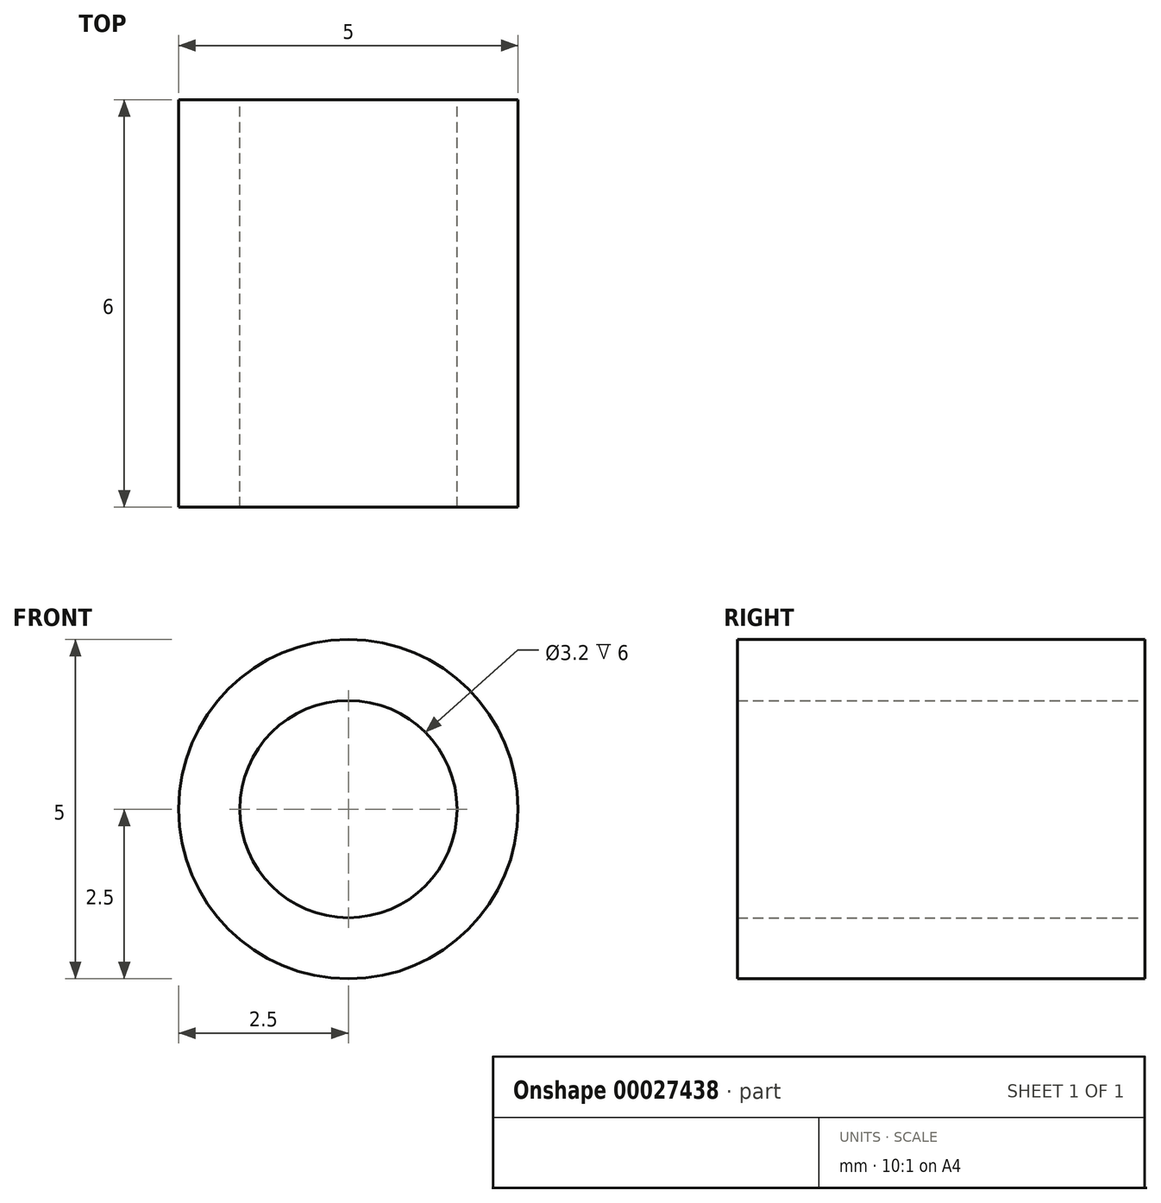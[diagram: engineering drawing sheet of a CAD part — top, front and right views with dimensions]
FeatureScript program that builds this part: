
annotation { "Feature Type Name" : "Feature", "Feature Type Description" : "" }
export const myFeature = defineFeature(function(context is Context, id is Id, definition is map)
    precondition{}
    {
        {
            var Q0;
            Q0=qCreatedBy(makeId("Front.planeOp"),FACE);
            var sketch = newSketch(context, id + "F0", { "sketchPlane" : qUnion([Q0])});
            skCircle(sketch, "E0", {"center": v(0, 0) * mm, "radius": 2.5 * mm});
            skCircle(sketch, "E1", {"center": v(0, 0) * mm, "radius": 1.6 * mm});
            skSolve(sketch);
        }
        {
            var Q0;
            Q0=makeQuery(id+"F0.imprint","IMPRINT",FACE,{"disambiguationData":[TD([[makeQuery(id+"F0.imprint","IMPRINT",EDGE,{"derivedFrom":sQuery(id+"F0.wireOp",EDGE,"E0")}),1.0]])]});
            extrude(context, id + "F1", {"entities" : qUnion([Q0]), "depth" : 6 * mm});
        }
    });
